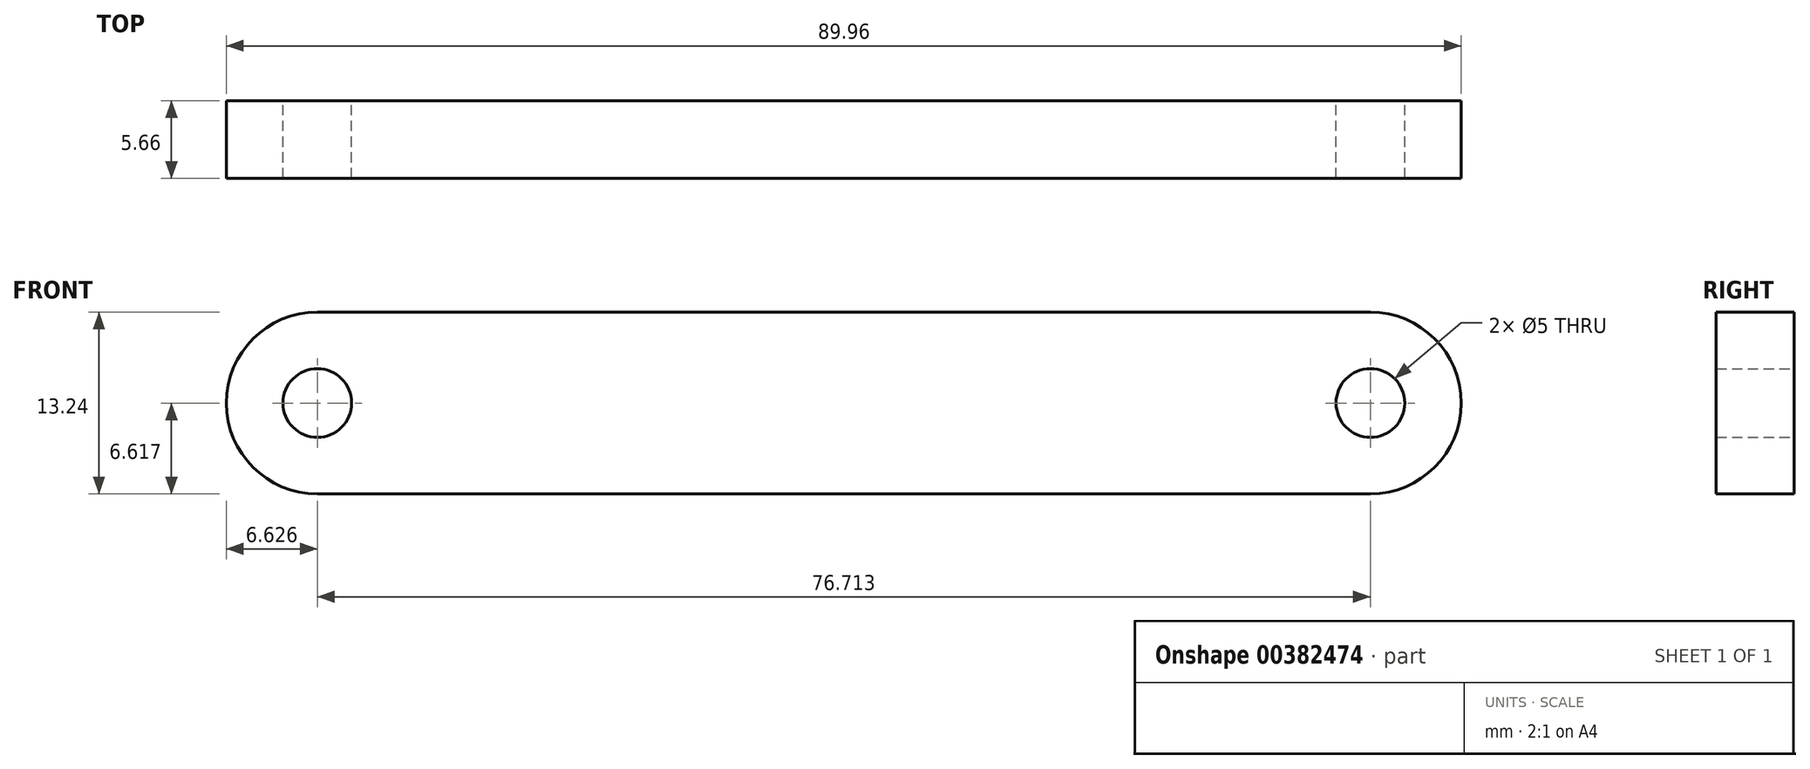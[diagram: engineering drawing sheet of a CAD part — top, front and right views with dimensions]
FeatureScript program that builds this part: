
annotation { "Feature Type Name" : "Feature", "Feature Type Description" : "" }
export const myFeature = defineFeature(function(context is Context, id is Id, definition is map)
    precondition{}
    {
        {
            var Q0;
            Q0=qCreatedBy(makeId("Front.planeOp"),FACE);
            var sketch = newSketch(context, id + "F0", { "sketchPlane" : qUnion([Q0])});
            skLineSegment(sketch, "E0", {"start": v(-31.45, 30.7) * mm, "end": v(45.26, 30.7) * mm});
            skArc(sketch, "E1", {"start": v(-31.45, 30.7) * mm, "mid": v(-38.08, 24.09) * mm, "end": v(-31.45, 17.47) * mm});
            skLineSegment(sketch, "E2", {"start": v(-31.45, 17.47) * mm, "end": v(45.26, 17.47) * mm});
            skArc(sketch, "E3", {"start": v(45.26, 30.7) * mm, "mid": v(51.88, 24.09) * mm, "end": v(45.26, 17.47) * mm});
            skCircle(sketch, "E4", {"center": v(-31.45, 24.09) * mm, "radius": 2.5 * mm});
            skCircle(sketch, "E5", {"center": v(45.26, 24.09) * mm, "radius": 2.5 * mm});
            skSolve(sketch);
        }
        {
            var Q0;
            Q0=makeQuery(id+"F0.imprint","IMPRINT",FACE,{"disambiguationData":[TD([[makeQuery(id+"F0.imprint","IMPRINT",EDGE,{"derivedFrom":sQuery(id+"F0.wireOp",EDGE,"E0")}),-1.0]])]});
            extrude(context, id + "F1", {"entities" : qUnion([Q0]), "depth" : 5.66 * mm});
        }
    });
